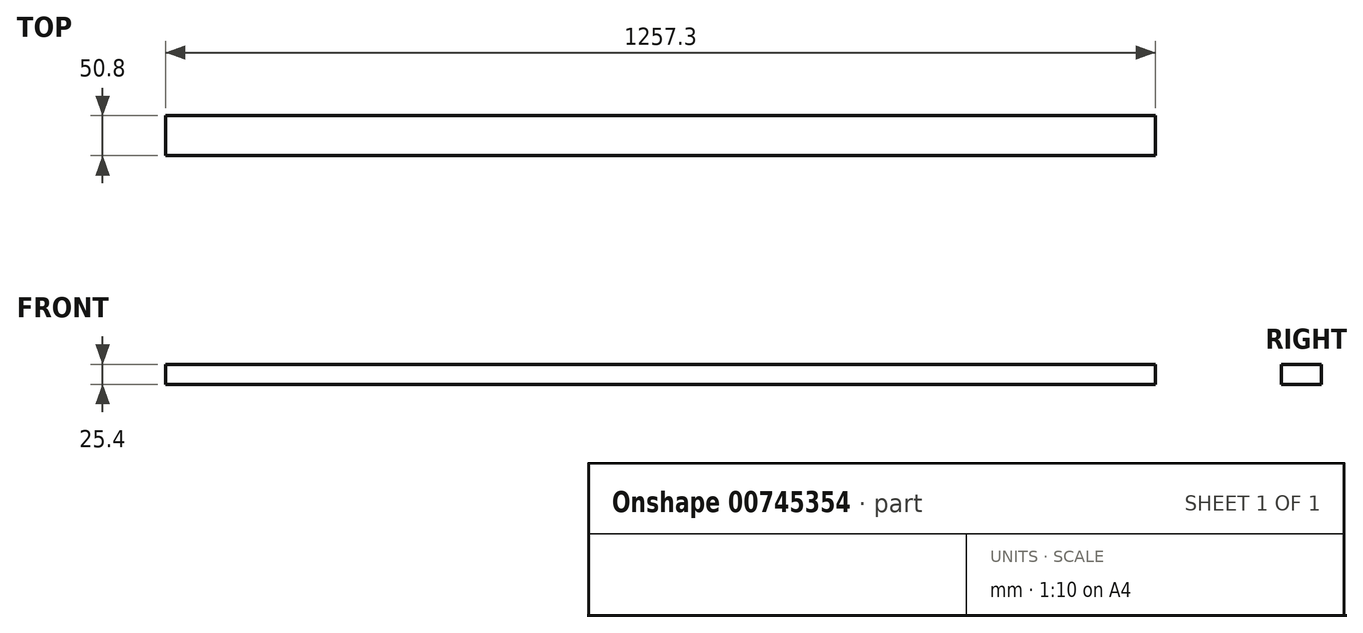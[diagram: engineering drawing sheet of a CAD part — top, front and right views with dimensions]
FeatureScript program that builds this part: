
annotation { "Feature Type Name" : "Feature", "Feature Type Description" : "" }
export const myFeature = defineFeature(function(context is Context, id is Id, definition is map)
    precondition{}
    {
        {
            var Q0;
            Q0=qCreatedBy(makeId("Top.planeOp"),FACE);
            var sketch = newSketch(context, id + "F0", { "sketchPlane" : qUnion([Q0])});
            skLineSegment(sketch, "E0.bottom", {"start": v(0, 0) * mm, "end": v(1257.3, 0) * mm});
            skLineSegment(sketch, "E0.top", {"start": v(0, 50.8) * mm, "end": v(1257.3, 50.8) * mm});
            skLineSegment(sketch, "E0.left", {"start": v(0, 0) * mm, "end": v(0, 50.8) * mm});
            skLineSegment(sketch, "E0.right", {"start": v(1257.3, 0) * mm, "end": v(1257.3, 50.8) * mm});
            skSolve(sketch);
        }
        {
            var Q0;
            Q0=makeQuery(id+"F0.imprint","IMPRINT",FACE,{"disambiguationData":[TD([[makeQuery(id+"F0.imprint","IMPRINT",EDGE,{"derivedFrom":sQuery(id+"F0.wireOp",EDGE,"XOJL2qkw-726g-F02Q-CQMI-GWsZiQ8f43vg.bottom")}),1.0]])]});
            var Q1;
            Q1=makeQuery(id+"F0.imprint","IMPRINT",FACE,{"disambiguationData":[TD([[makeQuery(id+"F0.imprint","IMPRINT",EDGE,{"derivedFrom":sQuery(id+"F0.wireOp",EDGE,"E0.bottom")}),1.0]])]});
            extrude(context, id + "F1", {"entities" : qUnion([Q0, Q1]), "depth" : 25.4 * mm, "offsetDistance" : 25.4 * mm});
        }
    });
